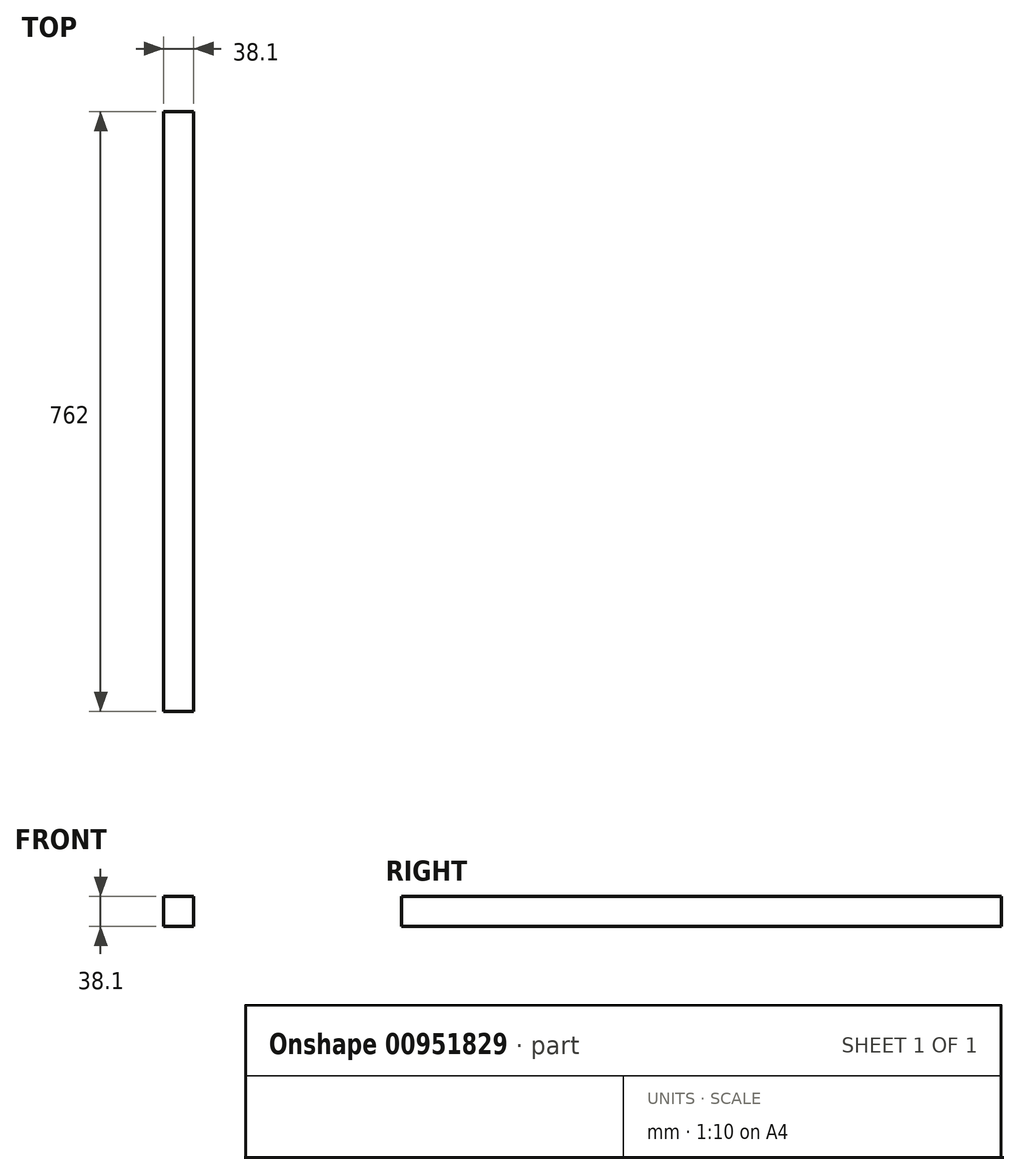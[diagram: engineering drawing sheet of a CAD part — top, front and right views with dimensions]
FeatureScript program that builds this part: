
annotation { "Feature Type Name" : "Feature", "Feature Type Description" : "" }
export const myFeature = defineFeature(function(context is Context, id is Id, definition is map)
    precondition{}
    {
        {
            var Q0;
            Q0=qCreatedBy(makeId("Front.planeOp"),FACE);
            var sketch = newSketch(context, id + "F0", { "sketchPlane" : qUnion([Q0])});
            skLineSegment(sketch, "E0.bottom", {"start": v(19.05, 19.05) * mm, "end": v(-19.05, 19.05) * mm});
            skLineSegment(sketch, "E0.top", {"start": v(19.05, -19.05) * mm, "end": v(-19.05, -19.05) * mm});
            skLineSegment(sketch, "E0.left", {"start": v(19.05, 19.05) * mm, "end": v(19.05, -19.05) * mm});
            skLineSegment(sketch, "E0.right", {"start": v(-19.05, 19.05) * mm, "end": v(-19.05, -19.05) * mm});
            skPoint(sketch, "E0.middle", {"position": v(0, 0) * mm});
            skSolve(sketch);
        }
        {
            var Q0;
            Q0 = qSketchRegion(id + "F0", true);
            extrude(context, id + "F1", {"entities" : qUnion([Q0]), "depth" : 381 * mm, "offsetDistance" : 25.4 * mm, "hasSecondDirection" : true, "secondDirectionOppositeDirection" : true, "secondDirectionDepth" : 381 * mm});
        }
    });
